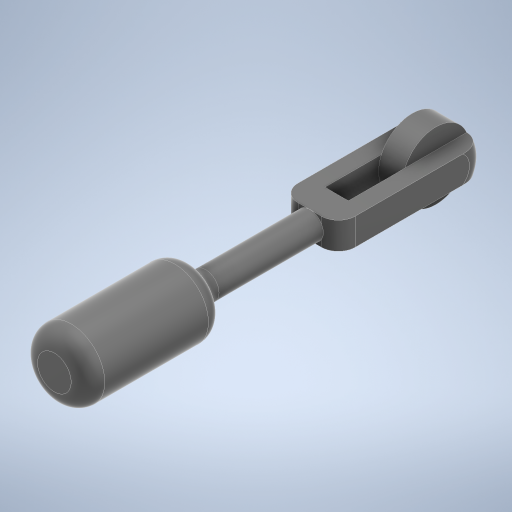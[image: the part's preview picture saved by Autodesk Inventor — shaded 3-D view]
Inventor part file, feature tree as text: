
AUTODESK INVENTOR PART (.ipt)
format: ipt  version: 2023 (Build 270158000, 158)  size: 346,112 bytes
history: native  units: mm
features: sketch x6, extrude x5, fillet x3, other x2, sweep x1
ambient origin geometry x8: Origin, YZ Plane, XZ Plane, XY Plane, X Axis, Y Axis, Z Axis, Center Point
bodies: Body1 (feature_tree)
feature tree (17):
  other  "솔리드1"
  extrude  "돌출1"  Depth=20.0mm
  extrude  "돌출2"  Depth=40.0mm TaperAngle=0.0deg
  sketch  "스케치3"
  other  "작업 평면1"
  sweep  "스윕1"
  sketch  "스케치6"
  fillet  "모깎기2"  Radius=40.0mm
  fillet  "모깎기4"  Radius=7.5mm
  extrude  "돌출4"  Depth=7.5mm
  extrude  "돌출3"  Depth=40.0mm
  extrude  "돌출6"  Depth=40.0mm
  fillet  "모깎기6"  Radius=8.0mm
  sketch  "스케치1"
  sketch  "스케치2"
  sketch  "스케치4"
  sketch  "스케치9"
